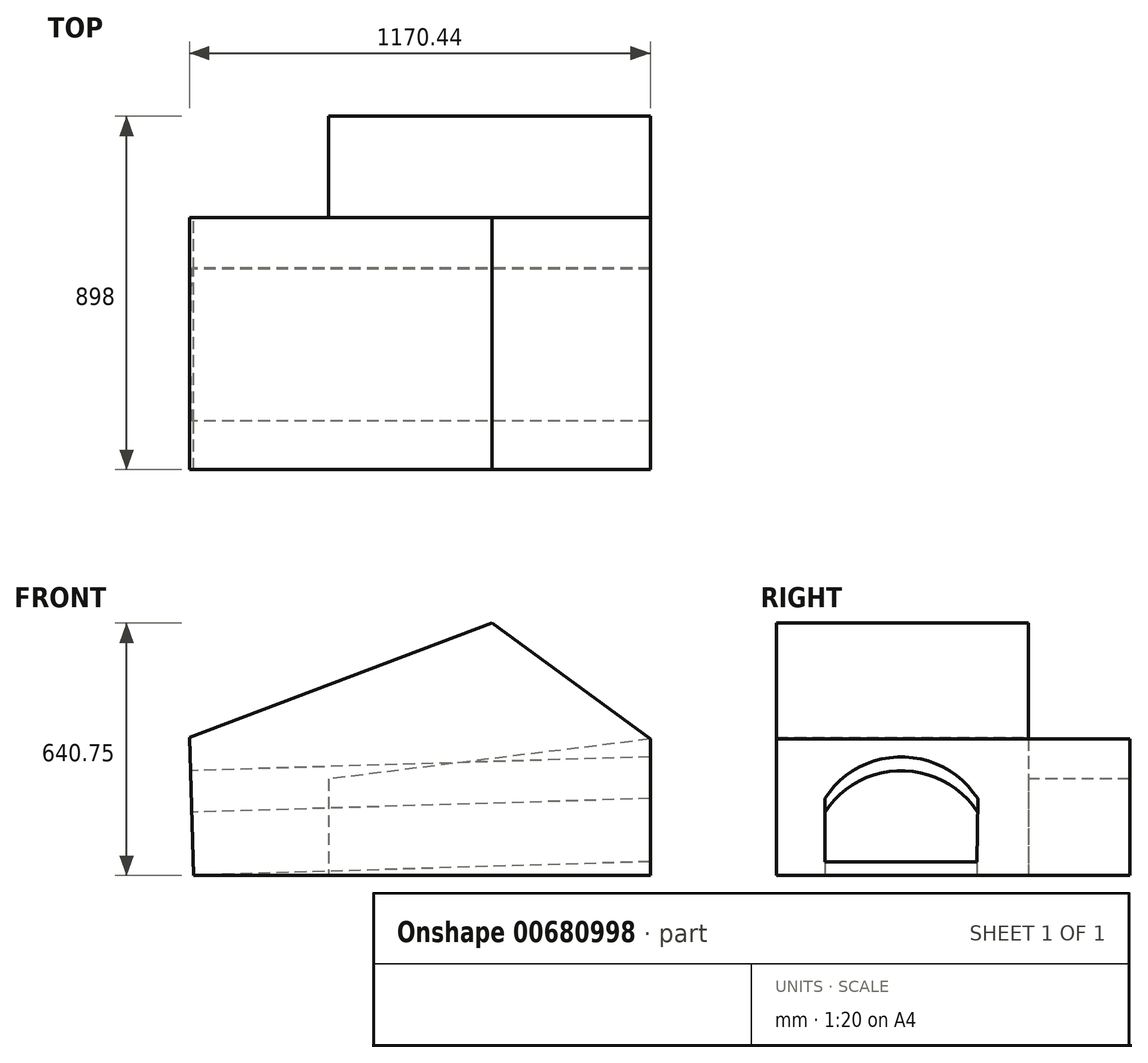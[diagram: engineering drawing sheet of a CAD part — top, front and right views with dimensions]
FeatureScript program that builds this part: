
annotation { "Feature Type Name" : "Feature", "Feature Type Description" : "" }
export const myFeature = defineFeature(function(context is Context, id is Id, definition is map)
    precondition{}
    {
        {
            var Q0;
            Q0=qCreatedBy(makeId("Front.planeOp"),FACE);
            var sketch = newSketch(context, id + "F0", { "sketchPlane" : qUnion([Q0])});
            skLineSegment(sketch, "E0", {"start": v(-565.89, -378.46) * mm, "end": v(594.11, -378.46) * mm});
            skLineSegment(sketch, "E1", {"start": v(594.11, -378.46) * mm, "end": v(594.11, -32.2) * mm});
            skLineSegment(sketch, "E2", {"start": v(594.11, -32.2) * mm, "end": v(192.21, 262.29) * mm});
            skLineSegment(sketch, "E3", {"start": v(192.21, 262.29) * mm, "end": v(-576.33, -28.61) * mm});
            skLineSegment(sketch, "E4", {"start": v(-576.33, -28.61) * mm, "end": v(-565.89, -378.46) * mm});
            skSolve(sketch);
        }
        {
            var Q0;
            Q0=makeQuery(id+"F0.imprint","IMPRINT",FACE,{"disambiguationData":[TD([[makeQuery(id+"F0.imprint","IMPRINT",EDGE,{"derivedFrom":sQuery(id+"F0.wireOp",EDGE,"E0")}),1.0]])]});
            extrude(context, id + "F1", {"entities" : qUnion([Q0]), "depth" : 640 * mm, "offsetDistance" : 25 * mm});
        }
        {
            var Q0;
            Q0=makeQuery(id+"F1.opExtrude","CAP_FACE",FACE,{"disambiguationData":[OSD([sQuery(id+"F0.wireOp",EDGE,"E0"),sQuery(id+"F0.wireOp",EDGE,"E1"),sQuery(id+"F0.wireOp",EDGE,"E2"),sQuery(id+"F0.wireOp",EDGE,"E3"),sQuery(id+"F0.wireOp",EDGE,"E4")])],"isStart":true});
            var sketch = newSketch(context, id + "F2", { "sketchPlane" : qUnion([Q0])});
            skLineSegment(sketch, "E5", {"start": v(-594.11, -32.2) * mm, "end": v(223.53, -133.72) * mm});
            skLineSegment(sketch, "E6", {"start": v(223.53, -133.72) * mm, "end": v(223.53, -378.46) * mm});
            skLineSegment(sketch, "E7", {"start": v(223.53, -378.46) * mm, "end": v(-594.11, -378.46) * mm});
            skLineSegment(sketch, "E8", {"start": v(-594.11, -378.46) * mm, "end": v(-594.11, -32.2) * mm});
            skSolve(sketch);
        }
        {
            var Q0;
            Q0=makeQuery(id+"F2.imprint","IMPRINT",FACE,{"disambiguationData":[TD([[makeQuery(id+"F2.imprint","IMPRINT",EDGE,{"derivedFrom":sQuery(id+"F2.wireOp",EDGE,"E5")}),-1.0]])]});
            extrude(context, id + "F3", {"entities" : qUnion([Q0]), "operationType" : NewBodyOperationType.ADD, "depth" : 258 * mm, "offsetDistance" : 25 * mm});
        }
        {
            var Q0;
            Q0=makeQuery(id+"F1.opExtrude","SWEPT_FACE",FACE,{"disambiguationData":[OSD([sQuery(id+"F0.wireOp",EDGE,"E4")])]});
            var sketch = newSketch(context, id + "F4", { "sketchPlane" : qUnion([Q0])});
            skLineSegment(sketch, "E9", {"start": v(130.76, -361.4) * mm, "end": v(517.02, -361.4) * mm});
            skLineSegment(sketch, "E10", {"start": v(517.02, -361.4) * mm, "end": v(517.02, -201.15) * mm});
            skArc(sketch, "E11", {"start": v(517.02, -201.15) * mm, "mid": v(322.74, -95.4) * mm, "end": v(128.46, -201.15) * mm});
            skLineSegment(sketch, "E12", {"start": v(128.46, -201.15) * mm, "end": v(130.76, -361.4) * mm});
            skSolve(sketch);
        }
        {
            var Q0;
            Q0=makeQuery(id+"F4.imprint","IMPRINT",FACE,{"disambiguationData":[TD([[makeQuery(id+"F4.imprint","IMPRINT",EDGE,{"derivedFrom":sQuery(id+"F4.wireOp",EDGE,"E9")}),-1.0]])]});
            extrude(context, id + "F5", {"entities" : qUnion([Q0]), "operationType" : NewBodyOperationType.REMOVE, "oppositeDirection" : true, "depth" : 1440 * mm, "offsetDistance" : 25 * mm});
        }
    });
